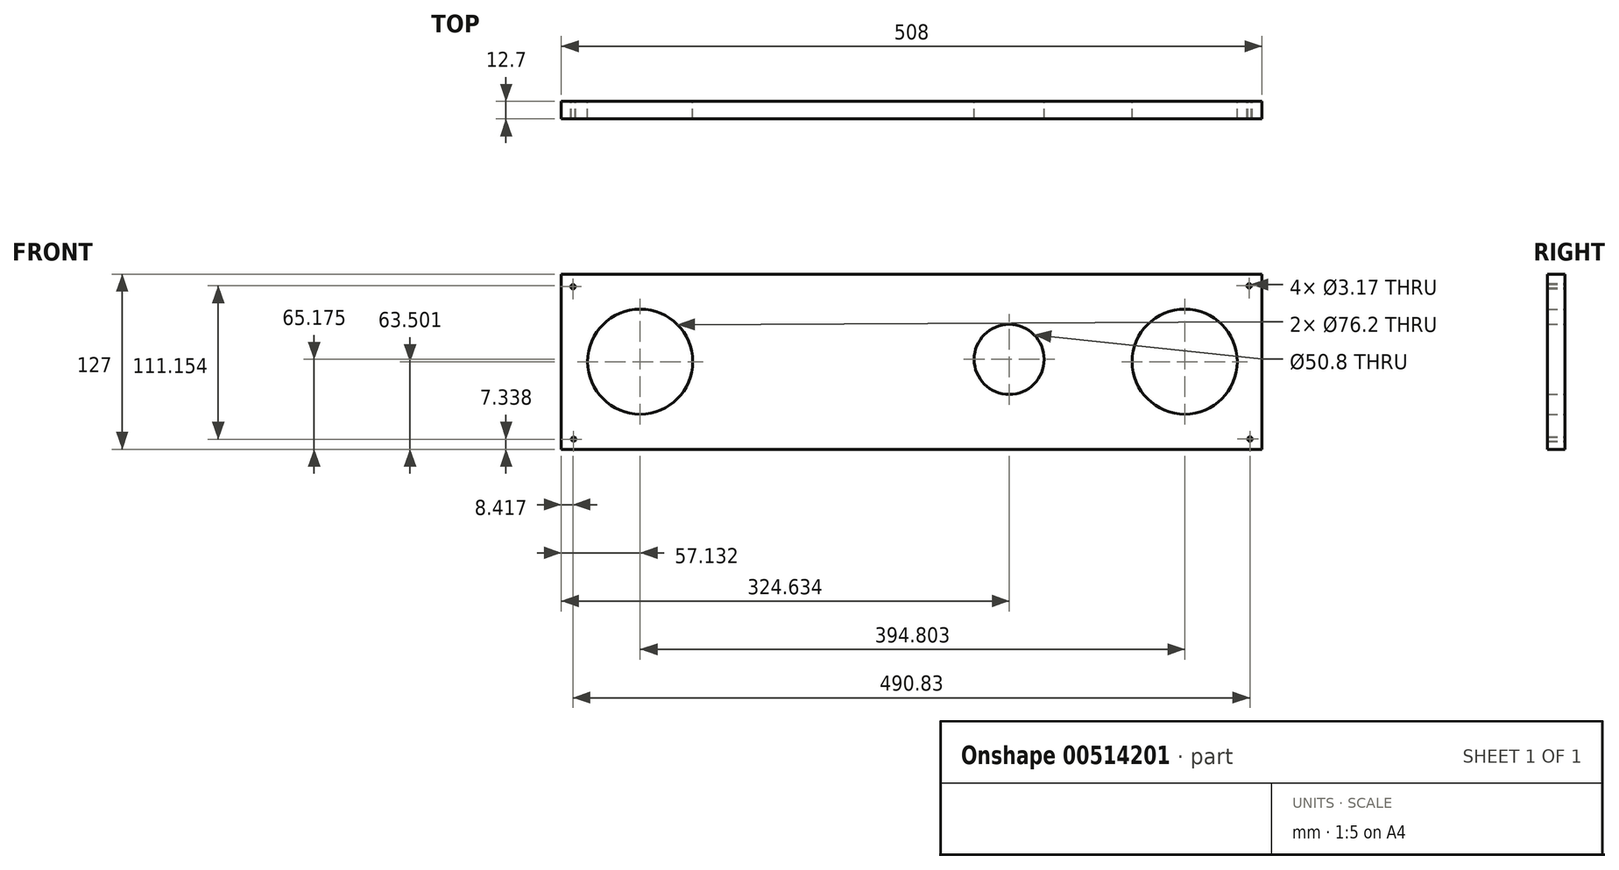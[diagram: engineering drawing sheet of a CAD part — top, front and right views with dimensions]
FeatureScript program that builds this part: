
annotation { "Feature Type Name" : "Feature", "Feature Type Description" : "" }
export const myFeature = defineFeature(function(context is Context, id is Id, definition is map)
    precondition{}
    {
        {
            var Q0;
            Q0=qCreatedBy(makeId("Front.planeOp"),FACE);
            var sketch = newSketch(context, id + "F0", { "sketchPlane" : qUnion([Q0])});
            skLineSegment(sketch, "E0.bottom", {"start": v(-397.87, 115.2) * mm, "end": v(110.13, 115.2) * mm});
            skLineSegment(sketch, "E0.top", {"start": v(-397.87, -11.8) * mm, "end": v(110.13, -11.8) * mm});
            skLineSegment(sketch, "E0.left", {"start": v(-397.87, 115.2) * mm, "end": v(-397.87, -11.8) * mm});
            skLineSegment(sketch, "E0.right", {"start": v(110.13, 115.2) * mm, "end": v(110.13, -11.8) * mm});
            skSolve(sketch);
        }
        {
            var Q0;
            Q0 = qSketchRegion(id + "F0", true);
            extrude(context, id + "F1", {"entities" : qUnion([Q0]), "depth" : 12.7 * mm, "offsetDistance" : 25.4 * mm});
        }
        {
            var Q0;
            Q0=makeQuery(id+"F1.opExtrude","CAP_FACE",FACE,{"disambiguationData":[OSD([sQuery(id+"F0.wireOp",EDGE,"E0.bottom"),sQuery(id+"F0.wireOp",EDGE,"E0.top"),sQuery(id+"F0.wireOp",EDGE,"E0.left"),sQuery(id+"F0.wireOp",EDGE,"E0.right")])],"isStart":false});
            var sketch = newSketch(context, id + "F2", { "sketchPlane" : qUnion([Q0])});
            skCircle(sketch, "E1", {"center": v(-388.95, 104.96) * mm, "radius": 3.18 * mm});
            skCircle(sketch, "E2", {"center": v(-387.54, 0) * mm, "radius": 3.18 * mm});
            skCircle(sketch, "E3", {"center": v(100.73, 106.68) * mm, "radius": 3.18 * mm});
            skCircle(sketch, "E4", {"center": v(100.26, 0) * mm, "radius": 3.18 * mm});
            skCircle(sketch, "E5", {"center": v(-345.01, 52.12) * mm, "radius": 38.1 * mm});
            skCircle(sketch, "E6", {"center": v(56.9, 53.14) * mm, "radius": 38.87 * mm});
            skSolve(sketch);
        }
        {
            var Q0;
            Q0=sQuery(id+"F2.wireOp",VERTEX,"E3.center");
            var Q1;
            Q1=makeQuery(id+"F1.opExtrude","SWEPT_BODY",BODY,{"disambiguationData":[OSD([sQuery(id+"F0.wireOp",EDGE,"E0.bottom"),sQuery(id+"F0.wireOp",EDGE,"E0.top"),sQuery(id+"F0.wireOp",EDGE,"E0.left"),sQuery(id+"F0.wireOp",EDGE,"E0.right")])]});
            hole(context, id + "F3", {"style" : HoleStyle.SIMPLE, "endStyle" : HoleEndStyle.THROUGH, "holeDiameter" : 3.17 * mm, "isTappedThrough" : true, "tappedDepth" : 12.7 * mm, "tapClearance" : 3, "locations" : qUnion([Q0]), "scope" : qUnion([Q1])});
        }
        {
            var Q0;
            Q0=makeQuery(id+"F1.opExtrude","CAP_FACE",FACE,{"disambiguationData":[OSD([sQuery(id+"F0.wireOp",EDGE,"E0.bottom"),sQuery(id+"F0.wireOp",EDGE,"E0.top"),sQuery(id+"F0.wireOp",EDGE,"E0.left"),sQuery(id+"F0.wireOp",EDGE,"E0.right")])],"isStart":false});
            var sketch = newSketch(context, id + "F4", { "sketchPlane" : qUnion([Q0])});
            skCircle(sketch, "E7", {"center": v(-389.45, 106.04) * mm, "radius": 3.18 * mm});
            skCircle(sketch, "E8", {"center": v(-389, -4.47) * mm, "radius": 3.18 * mm});
            skCircle(sketch, "E9", {"center": v(101.38, -4.36) * mm, "radius": 3.18 * mm});
            skCircle(sketch, "E10", {"center": v(-340.88, 55.19) * mm, "radius": 34.06 * mm});
            skCircle(sketch, "E11", {"center": v(50.5, 50.2) * mm, "radius": 38.1 * mm});
            skSolve(sketch);
        }
        {
            var Q0;
            Q0=sQuery(id+"F4.wireOp",VERTEX,"E9.center");
            var Q1;
            Q1=sQuery(id+"F4.wireOp",VERTEX,"E7.center");
            var Q2;
            Q2=sQuery(id+"F4.wireOp",VERTEX,"E8.center");
            var Q3;
            Q3=makeQuery(id+"F1.opExtrude","SWEPT_BODY",BODY,{"disambiguationData":[OSD([sQuery(id+"F0.wireOp",EDGE,"E0.bottom"),sQuery(id+"F0.wireOp",EDGE,"E0.top"),sQuery(id+"F0.wireOp",EDGE,"E0.left"),sQuery(id+"F0.wireOp",EDGE,"E0.right")])]});
            hole(context, id + "F5", {"style" : HoleStyle.SIMPLE, "endStyle" : HoleEndStyle.THROUGH, "holeDiameter" : 3.17 * mm, "isTappedThrough" : true, "tappedDepth" : 12.7 * mm, "tapClearance" : 3, "locations" : qUnion([Q0, Q1, Q2]), "scope" : qUnion([Q3])});
        }
        {
            var Q0;
            Q0=makeQuery(id+"F1.opExtrude","CAP_FACE",FACE,{"disambiguationData":[OSD([sQuery(id+"F0.wireOp",EDGE,"E0.bottom"),sQuery(id+"F0.wireOp",EDGE,"E0.top"),sQuery(id+"F0.wireOp",EDGE,"E0.left"),sQuery(id+"F0.wireOp",EDGE,"E0.right")])],"isStart":false});
            var sketch = newSketch(context, id + "F6", { "sketchPlane" : qUnion([Q0])});
            skCircle(sketch, "E12", {"center": v(-340.74, 51.7) * mm, "radius": 38.1 * mm});
            skCircle(sketch, "E13", {"center": v(48.46, 52.86) * mm, "radius": 38.1 * mm});
            skSolve(sketch);
        }
        {
            var Q0;
            Q0=sQuery(id+"F6.wireOp",VERTEX,"E12.center");
            var Q1;
            Q1=makeQuery(id+"F1.opExtrude","SWEPT_BODY",BODY,{"disambiguationData":[OSD([sQuery(id+"F0.wireOp",EDGE,"E0.bottom"),sQuery(id+"F0.wireOp",EDGE,"E0.top"),sQuery(id+"F0.wireOp",EDGE,"E0.left"),sQuery(id+"F0.wireOp",EDGE,"E0.right")])]});
            hole(context, id + "F7", {"style" : HoleStyle.SIMPLE, "endStyle" : HoleEndStyle.THROUGH, "holeDiameter" : 76.2 * mm, "isTappedThrough" : true, "tappedDepth" : 12.7 * mm, "tapClearance" : 3, "locations" : qUnion([Q0]), "scope" : qUnion([Q1])});
        }
        {
            var Q0;
            Q0=makeQuery(id+"F1.opExtrude","CAP_FACE",FACE,{"disambiguationData":[OSD([sQuery(id+"F0.wireOp",EDGE,"E0.bottom"),sQuery(id+"F0.wireOp",EDGE,"E0.top"),sQuery(id+"F0.wireOp",EDGE,"E0.left"),sQuery(id+"F0.wireOp",EDGE,"E0.right")])],"isStart":false});
            var sketch = newSketch(context, id + "F8", { "sketchPlane" : qUnion([Q0])});
            skCircle(sketch, "E14", {"center": v(-73.24, 53.37) * mm, "radius": 25.4 * mm});
            skSolve(sketch);
        }
        {
            var Q0;
            Q0=sQuery(id+"F8.wireOp",VERTEX,"E14.center");
            var Q1;
            Q1=makeQuery(id+"F1.opExtrude","SWEPT_BODY",BODY,{"disambiguationData":[OSD([sQuery(id+"F0.wireOp",EDGE,"E0.bottom"),sQuery(id+"F0.wireOp",EDGE,"E0.top"),sQuery(id+"F0.wireOp",EDGE,"E0.left"),sQuery(id+"F0.wireOp",EDGE,"E0.right")])]});
            hole(context, id + "F9", {"style" : HoleStyle.SIMPLE, "endStyle" : HoleEndStyle.THROUGH, "holeDiameter" : 50.8 * mm, "isTappedThrough" : true, "tappedDepth" : 12.7 * mm, "tapClearance" : 3, "locations" : qUnion([Q0]), "scope" : qUnion([Q1])});
        }
        {
            var Q0;
            Q0=makeQuery(id+"F1.opExtrude","CAP_FACE",FACE,{"disambiguationData":[OSD([sQuery(id+"F0.wireOp",EDGE,"E0.bottom"),sQuery(id+"F0.wireOp",EDGE,"E0.top"),sQuery(id+"F0.wireOp",EDGE,"E0.left"),sQuery(id+"F0.wireOp",EDGE,"E0.right")])],"isStart":false});
            var sketch = newSketch(context, id + "F10", { "sketchPlane" : qUnion([Q0])});
            skCircle(sketch, "E15", {"center": v(54.06, 51.7) * mm, "radius": 38.1 * mm});
            skPoint(sketch, "E15.centerSnap0", {"position": v(110.13, 51.7) * mm});
            skSolve(sketch);
        }
        {
            var Q0;
            Q0=sQuery(id+"F10.wireOp",VERTEX,"E15.center");
            var Q1;
            Q1=makeQuery(id+"F1.opExtrude","SWEPT_BODY",BODY,{"disambiguationData":[OSD([sQuery(id+"F0.wireOp",EDGE,"E0.bottom"),sQuery(id+"F0.wireOp",EDGE,"E0.top"),sQuery(id+"F0.wireOp",EDGE,"E0.left"),sQuery(id+"F0.wireOp",EDGE,"E0.right")])]});
            hole(context, id + "F11", {"style" : HoleStyle.SIMPLE, "endStyle" : HoleEndStyle.THROUGH, "holeDiameter" : 76.2 * mm, "isTappedThrough" : true, "tappedDepth" : 12.7 * mm, "tapClearance" : 3, "locations" : qUnion([Q0]), "scope" : qUnion([Q1])});
        }
    });
